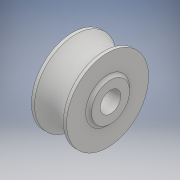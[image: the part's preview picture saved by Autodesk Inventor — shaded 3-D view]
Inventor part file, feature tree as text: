
AUTODESK INVENTOR PART (.ipt)
format: ipt  version: 2018 (Build 220112000, 112)  size: 174,080 bytes
history: native  units: mm
features: revolve x1, fillet x1, sketch x1
ambient origin geometry x8: Origin, YZ Plane, XZ Plane, XY Plane, X Axis, Y Axis, Z Axis, Center Point
bodies: Solid1 (feature_tree)
feature tree (3):
  revolve  "Revolution1"  [1 undecoded]
  fillet  "Fillet1"  Radius=26.0mm
  sketch  "Sketch1"  dims[d0=28.0mm d1=14.0mm d2=26.0mm d3=2.0mm d5=24.0mm d6=56.0mm d8=10.0mm d11=14.0mm d12=56.0mm d13=76.0mm d14=90.0deg d15=2.0mm]
note: 1 required parameter value undecoded (feature->parameter linkage not recoverable at this tier; creation-order binding heuristic only, values carry confidence <= 0.55)
